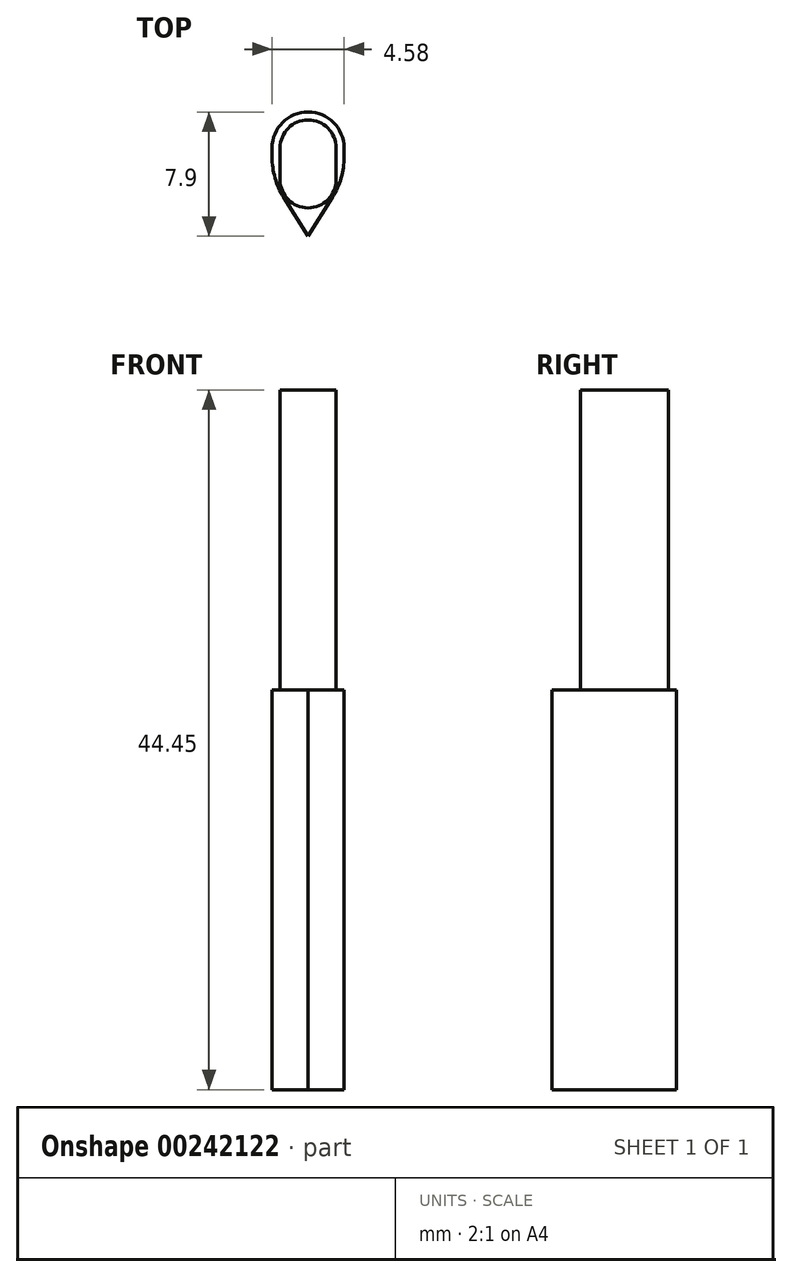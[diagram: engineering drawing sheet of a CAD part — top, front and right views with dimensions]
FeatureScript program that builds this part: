
annotation { "Feature Type Name" : "Feature", "Feature Type Description" : "" }
export const myFeature = defineFeature(function(context is Context, id is Id, definition is map)
    precondition{}
    {
        {
            var Q0;
            Q0=qCreatedBy(makeId("Top.planeOp"),FACE);
            var sketch = newSketch(context, id + "F0", { "sketchPlane" : qUnion([Q0])});
            skLineSegment(sketch, "E0", {"start": v(0, 1.02) * mm, "end": v(-2.54, 1.02) * mm, "construction": true});
            skLineSegment(sketch, "E1", {"start": v(0, 1.02) * mm, "end": v(2.54, 1.02) * mm, "construction": true});
            skPoint(sketch, "E2.visualSharp", {"position": v(2.54, -1.02) * mm});
            skPoint(sketch, "E3.visualSharp", {"position": v(-2.54, -1.02) * mm});
            skLineSegment(sketch, "E4.0", {"start": v(2.29, 1.02) * mm, "end": v(2.29, 0.44) * mm});
            skArc(sketch, "E4.1", {"start": v(1.55, -2.12) * mm, "mid": v(2.1, -0.89) * mm, "end": v(2.29, 0.44) * mm});
            skLineSegment(sketch, "E4.2", {"start": v(-2.29, 1.02) * mm, "end": v(-2.29, 0.44) * mm});
            skArc(sketch, "E4.3", {"start": v(-2.29, 0.44) * mm, "mid": v(-2.1, -0.89) * mm, "end": v(-1.55, -2.12) * mm});
            skLineSegment(sketch, "E4.4", {"start": v(-1.55, -2.12) * mm, "end": v(0, -4.6) * mm});
            skArc(sketch, "E4.5", {"start": v(2.29, 1.02) * mm, "mid": v(0, 3.3) * mm, "end": v(-2.29, 1.02) * mm});
            skLineSegment(sketch, "E4.6", {"start": v(0, -4.6) * mm, "end": v(1.55, -2.12) * mm});
            skPoint(sketch, "E5.end.orphan", {"position": v(0, -5.08) * mm});
            skSolve(sketch);
        }
        {
            var Q0;
            Q0 = qSketchRegion(id + "F0", true);
            extrude(context, id + "F1", {"entities" : qUnion([Q0]), "depth" : 25.4 * mm});
        }
        {
            var Q0;
            Q0=makeQuery(id+"F1.opExtrude","CAP_FACE",FACE,{"disambiguationData":[OSD([sQuery(id+"F0.wireOp",EDGE,"E4.0"),sQuery(id+"F0.wireOp",EDGE,"E4.1"),sQuery(id+"F0.wireOp",EDGE,"E4.2"),sQuery(id+"F0.wireOp",EDGE,"E4.3"),sQuery(id+"F0.wireOp",EDGE,"E4.4"),sQuery(id+"F0.wireOp",EDGE,"E4.5"),sQuery(id+"F0.wireOp",EDGE,"E4.6")])],"isStart":false});
            var sketch = newSketch(context, id + "F2", { "sketchPlane" : qUnion([Q0])});
            skLineSegment(sketch, "E6.0", {"start": v(-1.78, 1.02) * mm, "end": v(-1.78, -1.02) * mm});
            skArc(sketch, "E6.1", {"start": v(1.78, 1.02) * mm, "mid": v(0, 2.8) * mm, "end": v(-1.78, 1.02) * mm});
            skLineSegment(sketch, "E6.2", {"start": v(1.78, 1.02) * mm, "end": v(1.78, -1.02) * mm});
            skArc(sketch, "E6.3", {"start": v(-1.78, -1.02) * mm, "mid": v(0, -2.8) * mm, "end": v(1.78, -1.02) * mm});
            skPoint(sketch, "E7.start.orphan", {"position": v(-2.03, 1.02) * mm});
            skPoint(sketch, "E8.start.orphan", {"position": v(2.03, 1.02) * mm});
            skSolve(sketch);
        }
        {
            var Q0;
            Q0 = qSketchRegion(id + "F2", true);
            extrude(context, id + "F3", {"entities" : qUnion([Q0]), "operationType" : NewBodyOperationType.ADD, "depth" : 19.05 * mm});
        }
    });
